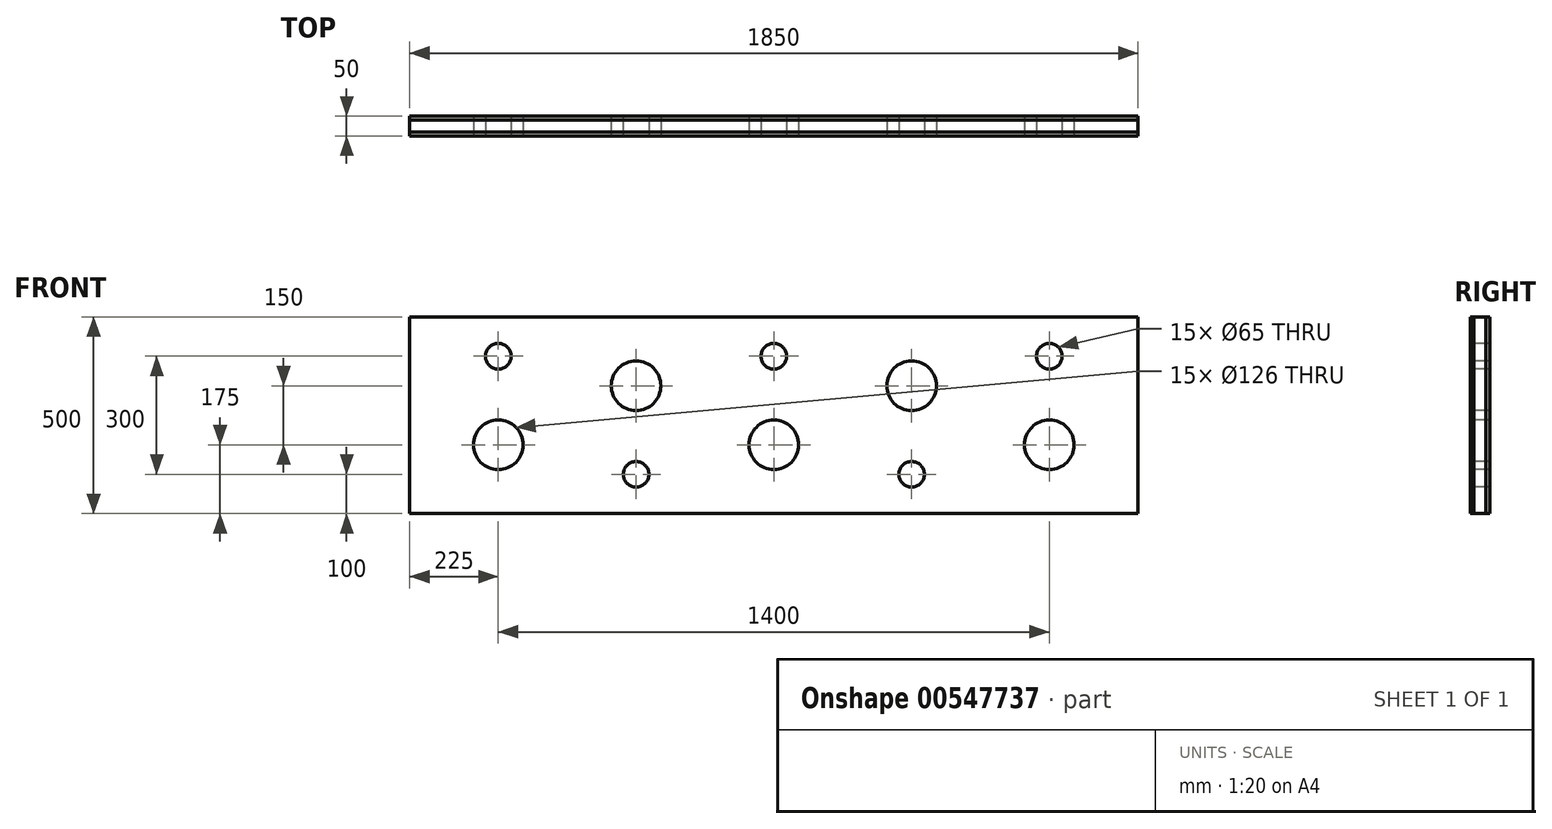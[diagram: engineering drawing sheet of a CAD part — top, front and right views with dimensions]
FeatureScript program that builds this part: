
annotation { "Feature Type Name" : "Feature", "Feature Type Description" : "" }
export const myFeature = defineFeature(function(context is Context, id is Id, definition is map)
    precondition{}
    {
        {
            var Q0;
            Q0=qCreatedBy(makeId("Top.planeOp"),FACE);
            var sketch = newSketch(context, id + "F0", { "sketchPlane" : qUnion([Q0])});
            skLineSegment(sketch, "E0.bottom", {"start": v(925, 15) * mm, "end": v(-925, 15) * mm});
            skLineSegment(sketch, "E0.top", {"start": v(925, -15) * mm, "end": v(-925, -15) * mm});
            skLineSegment(sketch, "E0.left", {"start": v(925, 15) * mm, "end": v(925, -15) * mm});
            skLineSegment(sketch, "E0.right", {"start": v(-925, 15) * mm, "end": v(-925, -15) * mm});
            skPoint(sketch, "E0.middle", {"position": v(0, 0) * mm});
            skSolve(sketch);
        }
        {
            var Q0;
            Q0=qSketchRegion(id+"F0",true);
            extrude(context, id + "F1", {"entities" : qUnion([Q0]), "endBound" : BoundingType.SYMMETRIC, "depth" : 500 * mm, "offsetDistance" : 25 * mm});
        }
        {
            var Q0;
            Q0=makeQuery(id+"F1.opExtrude","SWEPT_FACE",FACE,{"disambiguationData":[OSD([sQuery(id+"F0.wireOp",EDGE,"E0.top")])]});
            var sketch = newSketch(context, id + "F2", { "sketchPlane" : qUnion([Q0])});
            skLineSegment(sketch, "E1.0", {"start": v(925, 250) * mm, "end": v(-925, 250) * mm});
            skLineSegment(sketch, "E2.0", {"start": v(-925, 250) * mm, "end": v(-925, -250) * mm});
            skLineSegment(sketch, "E3.0", {"start": v(925, -250) * mm, "end": v(-925, -250) * mm});
            skLineSegment(sketch, "E4.0", {"start": v(925, 250) * mm, "end": v(925, -250) * mm});
            skSolve(sketch);
        }
        {
            var Q0;
            Q0 = qSketchRegion(id + "F2", true);
            extrude(context, id + "F3", {"entities" : qUnion([Q0]), "depth" : 10 * mm, "offsetDistance" : 25 * mm});
        }
        {
            var Q0;
            Q0=makeQuery(id+"F1.opExtrude","SWEPT_FACE",FACE,{"disambiguationData":[OSD([sQuery(id+"F0.wireOp",EDGE,"E0.bottom")])]});
            var sketch = newSketch(context, id + "F4", { "sketchPlane" : qUnion([Q0])});
            skLineSegment(sketch, "E5.0", {"start": v(-925, 250) * mm, "end": v(925, 250) * mm});
            skLineSegment(sketch, "E6.0", {"start": v(-925, 250) * mm, "end": v(-925, -250) * mm});
            skLineSegment(sketch, "E7.0", {"start": v(-925, -250) * mm, "end": v(925, -250) * mm});
            skLineSegment(sketch, "E8.0", {"start": v(925, 250) * mm, "end": v(925, -250) * mm});
            skSolve(sketch);
        }
        {
            var Q0;
            Q0 = qSketchRegion(id + "F4", true);
            extrude(context, id + "F5", {"entities" : qUnion([Q0]), "depth" : 10 * mm, "offsetDistance" : 25 * mm});
        }
        {
            var Q0;
            Q0=makeQuery(id+"F1.opExtrude","SWEPT_FACE",FACE,{"disambiguationData":[OSD([sQuery(id+"F0.wireOp",EDGE,"E0.top")])]});
            var sketch = newSketch(context, id + "F6", { "sketchPlane" : qUnion([Q0])});
            skLineSegment(sketch, "E9", {"start": v(-925, 150) * mm, "end": v(925, 150) * mm, "construction": true});
            skLineSegment(sketch, "E10", {"start": v(-925, 0) * mm, "end": v(925, 0) * mm, "construction": true});
            skLineSegment(sketch, "E11", {"start": v(-925, -75) * mm, "end": v(925, -75) * mm, "construction": true});
            skLineSegment(sketch, "E12", {"start": v(-925, 75) * mm, "end": v(925, 75) * mm, "construction": true});
            skLineSegment(sketch, "E13", {"start": v(-925, -150) * mm, "end": v(925, -150) * mm, "construction": true});
            skLineSegment(sketch, "E14", {"start": v(0, 250) * mm, "end": v(0, -250) * mm, "construction": true});
            skLineSegment(sketch, "E15", {"start": v(-350, 250) * mm, "end": v(-350, -250) * mm, "construction": true});
            skLineSegment(sketch, "E16", {"start": v(350, 250) * mm, "end": v(350, -250) * mm, "construction": true});
            skLineSegment(sketch, "E17", {"start": v(-700, 250) * mm, "end": v(-700, -250) * mm, "construction": true});
            skLineSegment(sketch, "E18", {"start": v(700, 250) * mm, "end": v(700, -250) * mm, "construction": true});
            skCircle(sketch, "E19", {"center": v(-700, 150) * mm, "radius": 32.5 * mm});
            skCircle(sketch, "E20", {"center": v(-350, 75) * mm, "radius": 63 * mm});
            skCircle(sketch, "E21", {"center": v(-700, -75) * mm, "radius": 63 * mm});
            skCircle(sketch, "E22", {"center": v(-350, -150) * mm, "radius": 32.5 * mm});
            skCircle(sketch, "E23", {"center": v(0, 150) * mm, "radius": 32.5 * mm});
            skCircle(sketch, "E24", {"center": v(0, -75) * mm, "radius": 63 * mm});
            skCircle(sketch, "E25", {"center": v(350, 75) * mm, "radius": 63 * mm});
            skCircle(sketch, "E26", {"center": v(350, -150) * mm, "radius": 32.5 * mm});
            skCircle(sketch, "E27", {"center": v(700, 150) * mm, "radius": 32.5 * mm});
            skCircle(sketch, "E28", {"center": v(700, -75) * mm, "radius": 63 * mm});
            skSolve(sketch);
        }
        {
            var Q0;
            Q0 = qSketchRegion(id + "F6", true);
            extrude(context, id + "F7", {"entities" : qUnion([Q0]), "operationType" : NewBodyOperationType.REMOVE, "endBound" : BoundingType.SYMMETRIC, "oppositeDirection" : true, "depth" : 200 * mm, "offsetDistance" : 25 * mm});
        }
    });
